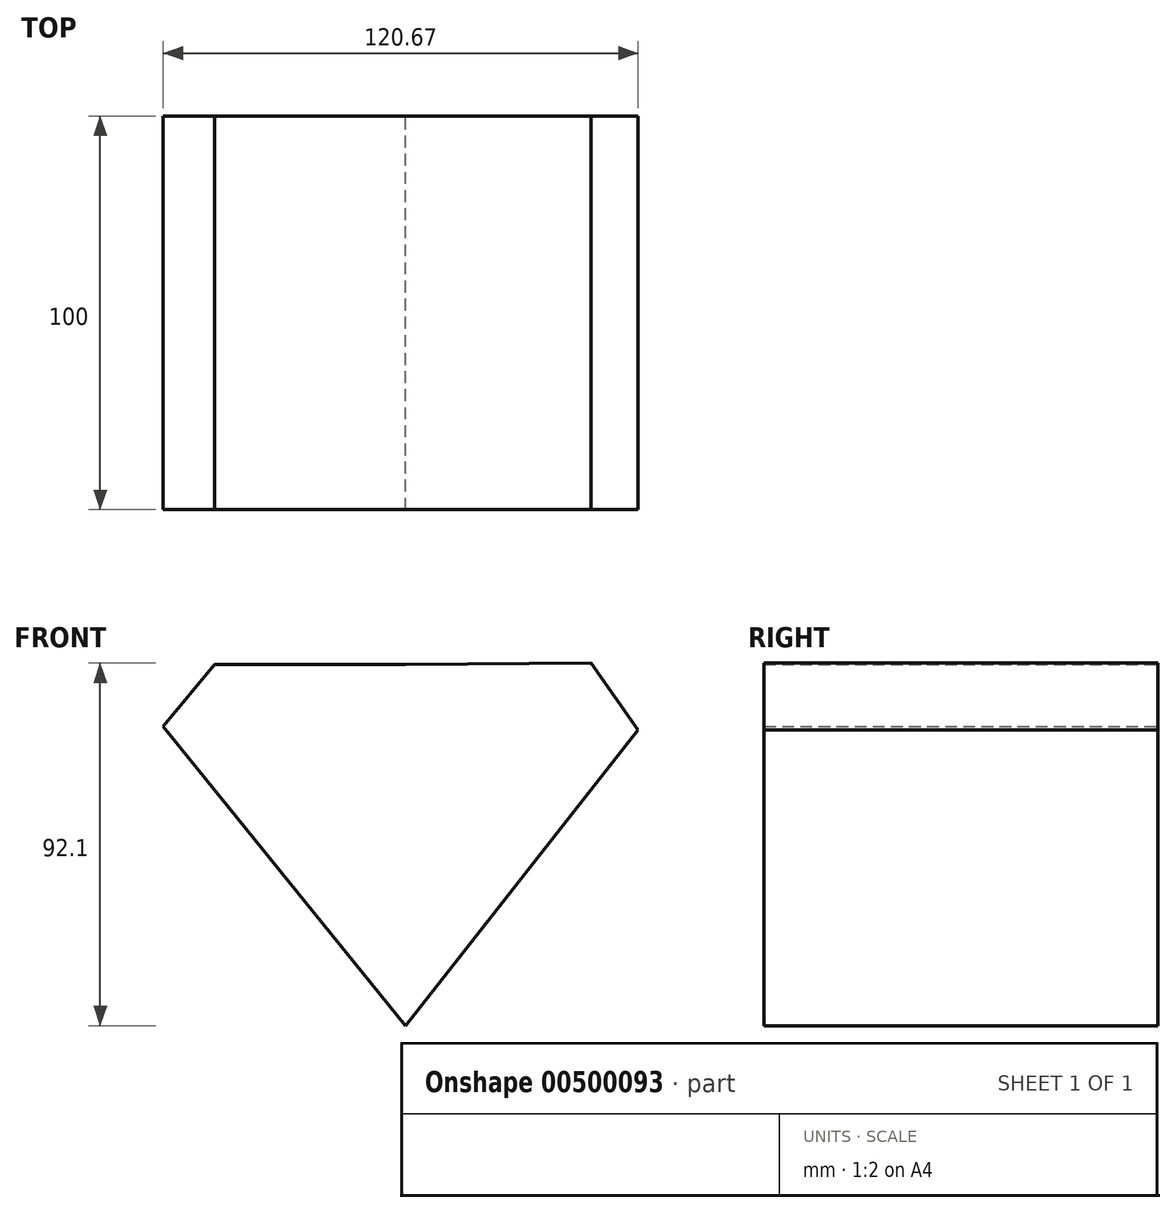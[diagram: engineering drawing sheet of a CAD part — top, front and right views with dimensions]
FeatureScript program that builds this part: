
annotation { "Feature Type Name" : "Feature", "Feature Type Description" : "" }
export const myFeature = defineFeature(function(context is Context, id is Id, definition is map)
    precondition{}
    {
        {
            var Q0;
            Q0=qCreatedBy(makeId("Front.planeOp"),FACE);
            var sketch = newSketch(context, id + "F0", { "sketchPlane" : qUnion([Q0])});
            skLineSegment(sketch, "E0", {"start": v(0, 36.58) * mm, "end": v(-48.38, 36.58) * mm});
            skLineSegment(sketch, "E1", {"start": v(-48.38, 36.58) * mm, "end": v(-61.5, 20.84) * mm});
            skLineSegment(sketch, "E2", {"start": v(-61.5, 20.84) * mm, "end": v(0, -55.23) * mm});
            skLineSegment(sketch, "E3", {"start": v(0, -55.23) * mm, "end": v(59.17, 19.97) * mm});
            skLineSegment(sketch, "E4", {"start": v(59.17, 19.97) * mm, "end": v(47.22, 36.87) * mm});
            skLineSegment(sketch, "E5", {"start": v(47.22, 36.87) * mm, "end": v(0, 36.58) * mm});
            skSolve(sketch);
        }
        {
            var Q0;
            Q0=makeQuery(id+"F0.imprint","IMPRINT",FACE,{"disambiguationData":[TD([[makeQuery(id+"F0.imprint","IMPRINT",EDGE,{"derivedFrom":sQuery(id+"F0.wireOp",EDGE,"E0")}),1.0]])]});
            extrude(context, id + "F1", {"entities" : qUnion([Q0]), "endBound" : BoundingType.SYMMETRIC, "depth" : 100 * mm});
        }
    });
